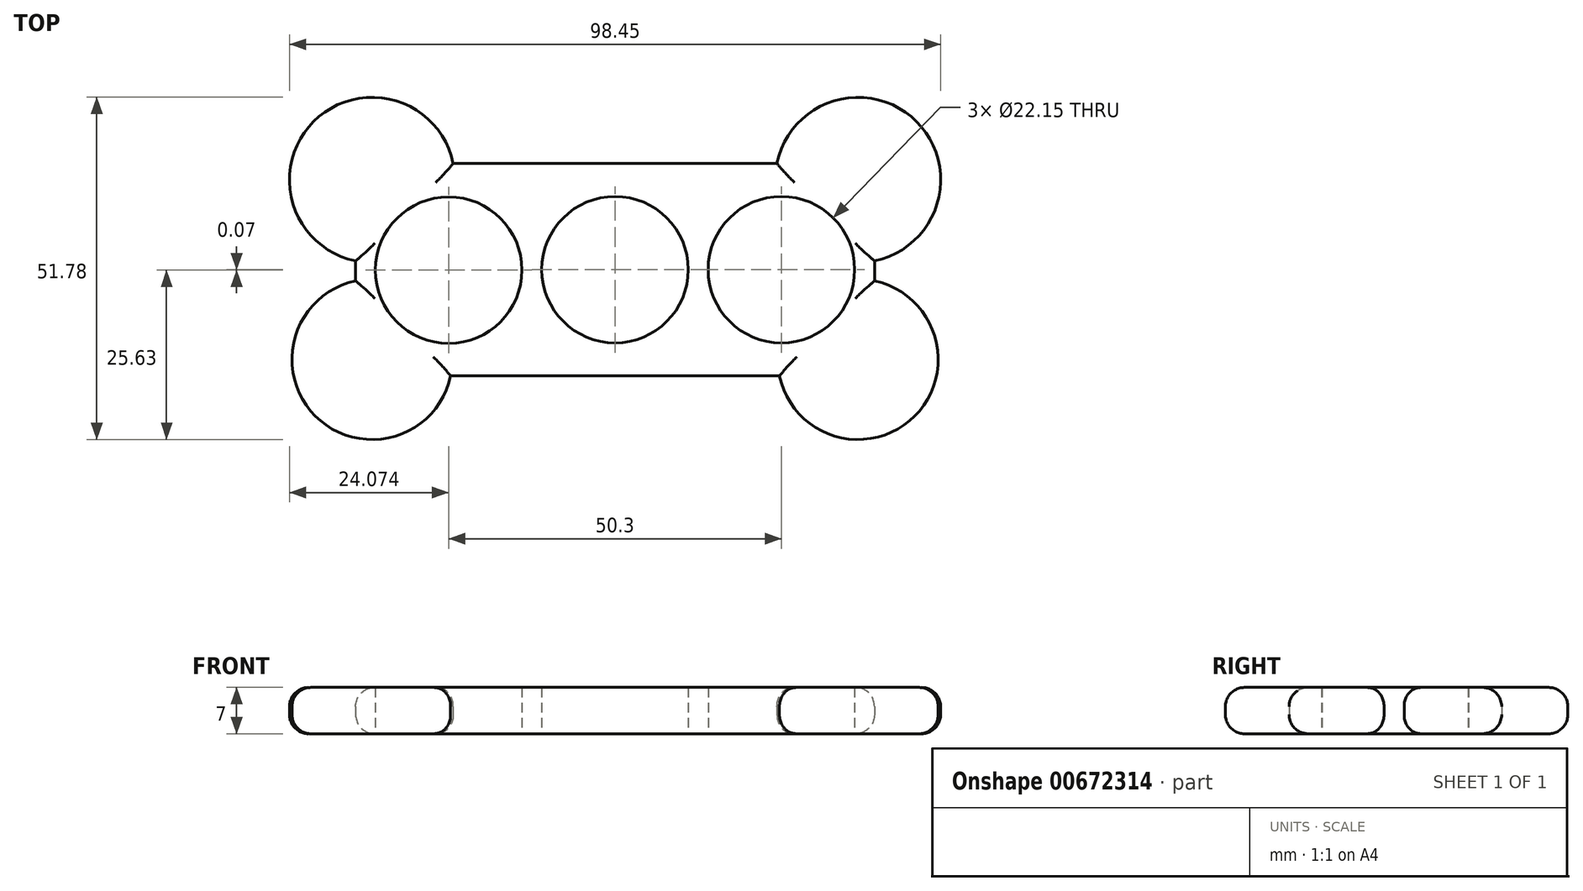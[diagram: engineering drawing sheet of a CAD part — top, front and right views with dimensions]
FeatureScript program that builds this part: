
annotation { "Feature Type Name" : "Feature", "Feature Type Description" : "" }
export const myFeature = defineFeature(function(context is Context, id is Id, definition is map)
    precondition{}
    {
        {
            var Q0;
            Q0=qCreatedBy(makeId("Top.planeOp"),FACE);
            var sketch = newSketch(context, id + "F0", { "sketchPlane" : qUnion([Q0])});
            skCircle(sketch, "E0", {"center": v(1.98, -0.04) * mm, "radius": 11.07 * mm});
            skCircle(sketch, "E1", {"center": v(27.13, -0.04) * mm, "radius": 11.07 * mm});
            skCircle(sketch, "E2", {"center": v(-23.17, -0.1) * mm, "radius": 11.07 * mm});
            skLineSegment(sketch, "E3.bottom", {"start": v(41.2, -16.11) * mm, "end": v(-37.24, -16.11) * mm});
            skLineSegment(sketch, "E3.top", {"start": v(41.2, 16.04) * mm, "end": v(-37.24, 16.04) * mm});
            skLineSegment(sketch, "E3.left", {"start": v(41.2, -16.11) * mm, "end": v(41.2, 16.04) * mm});
            skLineSegment(sketch, "E3.right", {"start": v(-37.24, -16.11) * mm, "end": v(-37.24, 16.04) * mm});
            skPoint(sketch, "E3.middle", {"position": v(-0.02, -0.04) * mm});
            skCircle(sketch, "E4", {"center": v(38.7, 13.54) * mm, "radius": 12.5 * mm});
            skCircle(sketch, "E5", {"center": v(38.7, -13.61) * mm, "radius": 12.13 * mm});
            skCircle(sketch, "E6", {"center": v(-34.74, 13.54) * mm, "radius": 12.5 * mm});
            skCircle(sketch, "E7", {"center": v(-34.74, -13.61) * mm, "radius": 12.13 * mm});
            skSolve(sketch);
        }
        {
            var Q0;
            {var subQ0=sQuery(id+"F0.wireOp",EDGE,"E3.right");var subQ1=sQuery(id+"F0.wireOp",EDGE,"E3.top");var subQ2=makeQuery(id+"F0.imprint","INTERSECT",VERTEX,{"derivedFrom":[subQ1,subQ0]});Q0=makeQuery(id+"F0.imprint","IMPRINT",FACE,{"disambiguationData":[TD([[makeQuery(id+"F0.imprint","IMPRINT",EDGE,{"disambiguationData":[TD([[subQ2,1.0]])],"derivedFrom":subQ1}),-1.0]])]});}
            var Q1;
            {var subQ3=sQuery(id+"F0.wireOp",EDGE,"E6");var subQ6=sQuery(id+"F0.wireOp",EDGE,"E2");var subQ7=makeQuery(id+"F0.imprint","INTERSECT",VERTEX,{"disambiguationData":[OD(0.0)],"derivedFrom":[subQ6,subQ3]});Q1=makeQuery(id+"F0.imprint","IMPRINT",FACE,{"disambiguationData":[TD([[makeQuery(id+"F0.imprint","IMPRINT",EDGE,{"disambiguationData":[TD([[subQ7,1.0]])],"derivedFrom":subQ6}),-1.0]])]});}
            var Q2;
            Q2=makeQuery(id+"F0.imprint","IMPRINT",FACE,{"disambiguationData":[TD([[makeQuery(id+"F0.imprint","IMPRINT",EDGE,{"derivedFrom":sQuery(id+"F0.wireOp",EDGE,"E0")}),-1.0]])]});
            var Q3;
            {var subQ0=sQuery(id+"F0.wireOp",EDGE,"E3.left");var subQ1=sQuery(id+"F0.wireOp",EDGE,"E3.top");var subQ2=makeQuery(id+"F0.imprint","INTERSECT",VERTEX,{"derivedFrom":[subQ1,subQ0]});Q3=makeQuery(id+"F0.imprint","IMPRINT",FACE,{"disambiguationData":[TD([[makeQuery(id+"F0.imprint","IMPRINT",EDGE,{"disambiguationData":[TD([[subQ2,-1.0]])],"derivedFrom":subQ1}),-1.0]])]});}
            var Q4;
            {var subQ3=sQuery(id+"F0.wireOp",EDGE,"E4");var subQ6=sQuery(id+"F0.wireOp",EDGE,"E1");var subQ7=makeQuery(id+"F0.imprint","INTERSECT",VERTEX,{"disambiguationData":[OD(0.0)],"derivedFrom":[subQ6,subQ3]});Q4=makeQuery(id+"F0.imprint","IMPRINT",FACE,{"disambiguationData":[TD([[makeQuery(id+"F0.imprint","IMPRINT",EDGE,{"disambiguationData":[TD([[subQ7,1.0]])],"derivedFrom":subQ6}),-1.0]])]});}
            var Q5;
            {var subQ0=sQuery(id+"F0.wireOp",EDGE,"E5");var subQ3=sQuery(id+"F0.wireOp",EDGE,"E1");var subQ5=makeQuery(id+"F0.imprint","INTERSECT",VERTEX,{"disambiguationData":[OD(0.0)],"derivedFrom":[subQ3,subQ0]});Q5=makeQuery(id+"F0.imprint","IMPRINT",FACE,{"disambiguationData":[TD([[makeQuery(id+"F0.imprint","IMPRINT",EDGE,{"disambiguationData":[TD([[subQ5,-1.0]])],"derivedFrom":subQ3}),-1.0]])]});}
            var Q6;
            {var subQ0=sQuery(id+"F0.wireOp",EDGE,"E3.left");var subQ1=sQuery(id+"F0.wireOp",EDGE,"E3.bottom");var subQ2=makeQuery(id+"F0.imprint","INTERSECT",VERTEX,{"derivedFrom":[subQ1,subQ0]});Q6=makeQuery(id+"F0.imprint","IMPRINT",FACE,{"disambiguationData":[TD([[makeQuery(id+"F0.imprint","IMPRINT",EDGE,{"disambiguationData":[TD([[subQ2,-1.0]])],"derivedFrom":subQ1}),1.0]])]});}
            var Q7;
            {var subQ0=sQuery(id+"F0.wireOp",EDGE,"E3.right");var subQ1=sQuery(id+"F0.wireOp",EDGE,"E3.bottom");var subQ2=makeQuery(id+"F0.imprint","INTERSECT",VERTEX,{"derivedFrom":[subQ1,subQ0]});Q7=makeQuery(id+"F0.imprint","IMPRINT",FACE,{"disambiguationData":[TD([[makeQuery(id+"F0.imprint","IMPRINT",EDGE,{"disambiguationData":[TD([[subQ2,1.0]])],"derivedFrom":subQ1}),1.0]])]});}
            var Q8;
            {var subQ0=sQuery(id+"F0.wireOp",EDGE,"E6");var subQ1=sQuery(id+"F0.wireOp",EDGE,"E2");var subQ2=makeQuery(id+"F0.imprint","INTERSECT",VERTEX,{"disambiguationData":[OD(0.0)],"derivedFrom":[subQ1,subQ0]});Q8=makeQuery(id+"F0.imprint","IMPRINT",FACE,{"disambiguationData":[TD([[makeQuery(id+"F0.imprint","IMPRINT",EDGE,{"disambiguationData":[TD([[subQ2,-1.0]])],"derivedFrom":subQ1}),-1.0]])]});}
            var Q9;
            {var subQ0=sQuery(id+"F0.wireOp",EDGE,"E7");var subQ3=sQuery(id+"F0.wireOp",EDGE,"E2");var subQ4=makeQuery(id+"F0.imprint","INTERSECT",VERTEX,{"disambiguationData":[OD(0.0)],"derivedFrom":[subQ3,subQ0]});Q9=makeQuery(id+"F0.imprint","IMPRINT",FACE,{"disambiguationData":[TD([[makeQuery(id+"F0.imprint","IMPRINT",EDGE,{"disambiguationData":[TD([[subQ4,-1.0]])],"derivedFrom":subQ3}),-1.0]])]});}
            var Q10;
            {var subQ0=sQuery(id+"F0.wireOp",EDGE,"E4");var subQ1=sQuery(id+"F0.wireOp",EDGE,"E1");var subQ2=makeQuery(id+"F0.imprint","INTERSECT",VERTEX,{"disambiguationData":[OD(1.0)],"derivedFrom":[subQ1,subQ0]});Q10=makeQuery(id+"F0.imprint","IMPRINT",FACE,{"disambiguationData":[TD([[makeQuery(id+"F0.imprint","IMPRINT",EDGE,{"disambiguationData":[TD([[subQ2,1.0]])],"derivedFrom":subQ1}),-1.0]])]});}
            extrude(context, id + "F1", {"entities" : qUnion([Q0, Q1, Q2, Q3, Q4, Q5, Q6, Q7, Q8, Q9, Q10]), "depth" : 7 * mm, "offsetDistance" : 25 * mm});
        }
        {
            var Q0;
            Q0=makeQuery(id+"F1.opExtrude","CAP_EDGE",EDGE,{"disambiguationData":[OSD([sQuery(id+"F0.wireOp",EDGE,"E7")])],"isStart":false});
            var Q1;
            Q1=makeQuery(id+"F1.opExtrude","CAP_EDGE",EDGE,{"disambiguationData":[OSD([sQuery(id+"F0.wireOp",EDGE,"E3.bottom")])],"isStart":false});
            var Q2;
            Q2=makeQuery(id+"F1.opExtrude","CAP_EDGE",EDGE,{"disambiguationData":[OSD([sQuery(id+"F0.wireOp",EDGE,"E5")])],"isStart":false});
            var Q3;
            Q3=makeQuery(id+"F1.opExtrude","CAP_EDGE",EDGE,{"disambiguationData":[OSD([sQuery(id+"F0.wireOp",EDGE,"E3.left")])],"isStart":false});
            var Q4;
            Q4=makeQuery(id+"F1.opExtrude","CAP_EDGE",EDGE,{"disambiguationData":[OSD([sQuery(id+"F0.wireOp",EDGE,"E4")])],"isStart":false});
            var Q5;
            Q5=makeQuery(id+"F1.opExtrude","CAP_EDGE",EDGE,{"disambiguationData":[OSD([sQuery(id+"F0.wireOp",EDGE,"E3.top")])],"isStart":false});
            var Q6;
            Q6=makeQuery(id+"F1.opExtrude","CAP_EDGE",EDGE,{"disambiguationData":[OSD([sQuery(id+"F0.wireOp",EDGE,"E6")])],"isStart":true});
            var Q7;
            Q7=makeQuery(id+"F1.opExtrude","CAP_EDGE",EDGE,{"disambiguationData":[OSD([sQuery(id+"F0.wireOp",EDGE,"E6")])],"isStart":false});
            var Q8;
            Q8=makeQuery(id+"F1.opExtrude","CAP_EDGE",EDGE,{"disambiguationData":[OSD([sQuery(id+"F0.wireOp",EDGE,"E3.right")])],"isStart":false});
            var Q9;
            Q9=makeQuery(id+"F1.opExtrude","CAP_EDGE",EDGE,{"disambiguationData":[OSD([sQuery(id+"F0.wireOp",EDGE,"E7")])],"isStart":true});
            var Q10;
            Q10=makeQuery(id+"F1.opExtrude","CAP_EDGE",EDGE,{"disambiguationData":[OSD([sQuery(id+"F0.wireOp",EDGE,"E3.right")])],"isStart":true});
            var Q11;
            Q11=makeQuery(id+"F1.opExtrude","CAP_EDGE",EDGE,{"disambiguationData":[OSD([sQuery(id+"F0.wireOp",EDGE,"E3.bottom")])],"isStart":true});
            var Q12;
            Q12=makeQuery(id+"F1.opExtrude","CAP_EDGE",EDGE,{"disambiguationData":[OSD([sQuery(id+"F0.wireOp",EDGE,"E3.top")])],"isStart":true});
            var Q13;
            Q13=makeQuery(id+"F1.opExtrude","CAP_EDGE",EDGE,{"disambiguationData":[OSD([sQuery(id+"F0.wireOp",EDGE,"E5")])],"isStart":true});
            var Q14;
            Q14=makeQuery(id+"F1.opExtrude","CAP_EDGE",EDGE,{"disambiguationData":[OSD([sQuery(id+"F0.wireOp",EDGE,"E4")])],"isStart":true});
            var Q15;
            Q15=makeQuery(id+"F1.opExtrude","CAP_EDGE",EDGE,{"disambiguationData":[OSD([sQuery(id+"F0.wireOp",EDGE,"E3.left")])],"isStart":true});
            fillet(context, id + "F2", {"entities" : qUnion([Q0, Q1, Q2, Q3, Q4, Q5, Q6, Q7, Q8, Q9, Q10, Q11, Q12, Q13, Q14, Q15]), "radius" : 2.9 * mm, "tangentPropagation" : true, "allowEdgeOverflow" : false});
        }
    });
